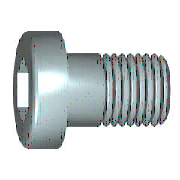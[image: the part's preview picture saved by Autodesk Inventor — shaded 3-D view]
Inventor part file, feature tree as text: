
AUTODESK INVENTOR PART (.ipt)
format: ipt  version: 2024 (Build 280153000, 153)  size: 189,952 bytes
history: native  units: mm (DEFAULTED — no unit token found)
features: other x3, extrude x1, plane x1
ambient origin geometry x7: Origin, YZ Plane, XY Plane, X Axis, Y Axis, Z Axis, Center Point
bodies: Solid1 (feature_tree)
feature tree (5):
  other  "Базовый элемент"
  other  "Фаска2"
  extrude  "Паз"  Depth=2.8mm
  other  "Work Axis1"
  plane  "Work Plane1"
